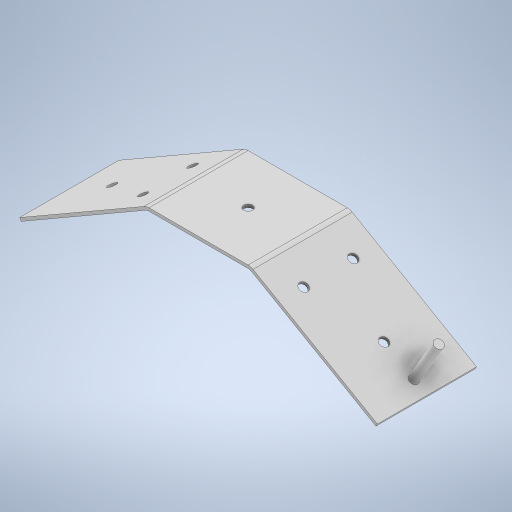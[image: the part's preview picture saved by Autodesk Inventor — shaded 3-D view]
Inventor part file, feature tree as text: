
AUTODESK INVENTOR PART (.ipt)
format: ipt  version: 2024 (Build 280153000, 153)  size: 301,568 bytes
history: native  units: mm
features: sketch x7, extrude x5, other x2
ambient origin geometry x8: Origin, YZ Plane, XZ Plane, XY Plane, X Axis, Y Axis, Z Axis, Center Point
bodies: Solid1 (feature_tree)
feature tree (14):
  extrude  "Extrusion1"  Depth=100.0mm
  other  "Bend Part1"
  other  "Bend Part2"
  extrude  "Extrusion2"  Depth=100.0mm
  extrude  "Extrusion3"  Depth=50.0mm
  extrude  "Extrusion4"  Depth=50.0mm
  extrude  "Extrusion5"  Depth=10.0mm
  sketch  "Sketch1"  dims[d0=400.0mm d1=100.0mm]
  sketch  "Sketch2"  dims[d2=3.0mm d3=0.0mm d4=100.0mm]
  sketch  "Sketch3"  dims[d5=50.0mm d6=50.0mm]
  sketch  "Sketch4"  dims[d7=10.0mm d8=30.0deg d9=50.0mm]
  sketch  "Sketch5"  dims[d10=10.0mm d11=30.0deg d12=9.0mm]
  sketch  "Sketch6"  dims[d13=5.0mm d14=0.0mm]
  sketch  "Sketch7"  dims[d15=9.0mm d16=9.0mm d17=50.0mm d18=25.0mm d19=30.0mm d20=30.0mm d21=5.0mm d22=0.0mm d23=9.0mm d24=9.0mm d25=25.0mm d26=50.0mm d27=30.0mm d28=30.0mm d29=5.0mm d30=0.0mm d31=9.0mm d32=50.0mm d33=50.0mm d34=9.0mm d35=50.0mm d36=50.0mm d37=9.0mm d38=50.0mm d44=35.0mm d45=9.0mm d46=15.0mm d47=50.0mm d48=50.0mm d49=0.0mm]
